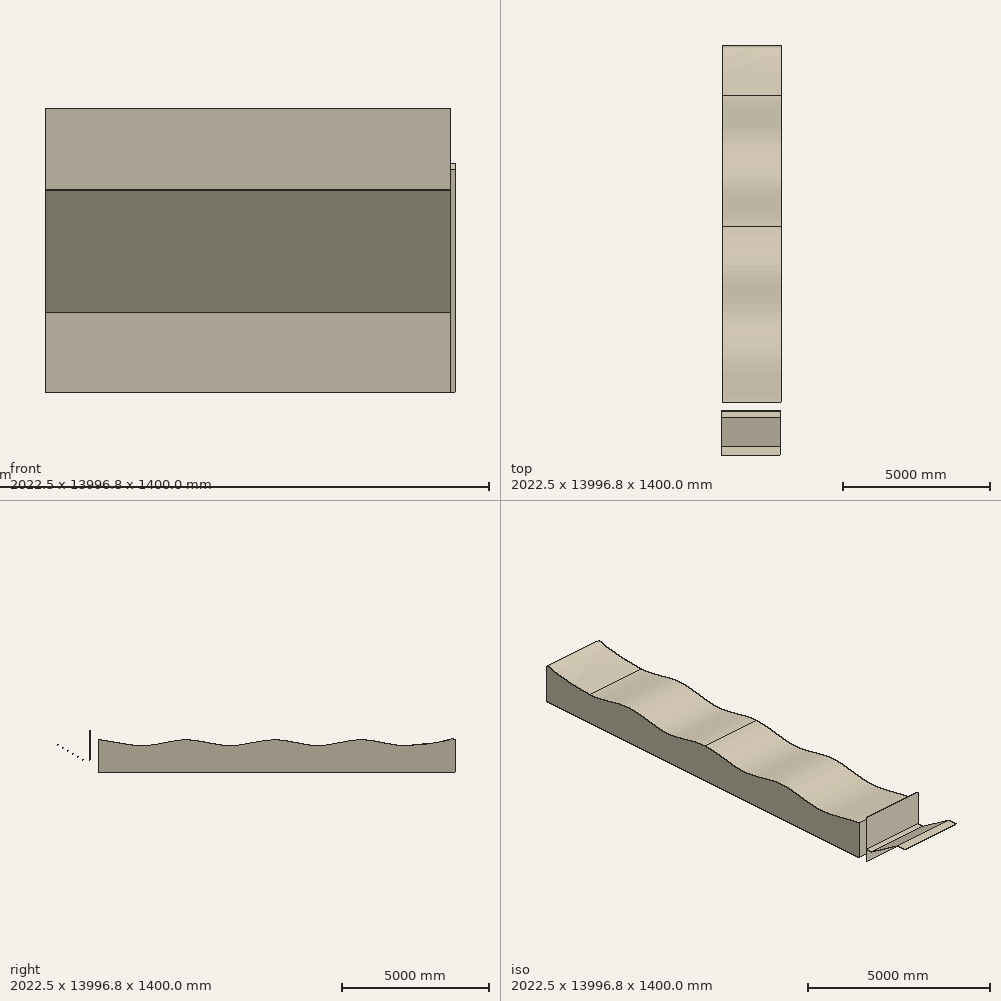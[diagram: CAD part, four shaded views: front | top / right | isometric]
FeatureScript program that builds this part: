
annotation { "Feature Type Name" : "Feature", "Feature Type Description" : "" }
export const myFeature = defineFeature(function(context is Context, id is Id, definition is map)
    precondition{}
    {
        {
            var Q0;
            Q0=qCreatedBy(makeId("Right.planeOp"),FACE);
            var sketch = newSketch(context, id + "F0", { "sketchPlane" : qUnion([Q0])});
            skLineSegment(sketch, "E0", {"start": v(0, 0) * mm, "end": v(0, 400) * mm});
            skLineSegment(sketch, "E1", {"start": v(0, 400) * mm, "end": v(-200, 400) * mm});
            skLineSegment(sketch, "E2", {"start": v(-200, 400) * mm, "end": v(-1200, 1000) * mm});
            skLineSegment(sketch, "E3", {"start": v(-1200, 1000) * mm, "end": v(-1500, 1000) * mm});
            skLineSegment(sketch, "E4.0", {"start": v(-1201.76, 993.65) * mm, "end": v(-1500, 993.65) * mm});
            skLineSegment(sketch, "E4.1", {"start": v(-201.76, 393.65) * mm, "end": v(-1201.76, 993.65) * mm});
            skLineSegment(sketch, "E4.2", {"start": v(-6.35, 393.65) * mm, "end": v(-201.76, 393.65) * mm});
            skLineSegment(sketch, "E4.3", {"start": v(-6.35, 0) * mm, "end": v(-6.35, 393.65) * mm});
            skLineSegment(sketch, "E5", {"start": v(-1500, 993.65) * mm, "end": v(-1500, 1000) * mm});
            skLineSegment(sketch, "E6", {"start": v(-6.35, 0) * mm, "end": v(0, 0) * mm});
            skSolve(sketch);
        }
        {
            var Q0;
            Q0=makeQuery(id+"F0.imprint","IMPRINT",FACE,{"disambiguationData":[TD([[makeQuery(id+"F0.imprint","IMPRINT",EDGE,{"derivedFrom":sQuery(id+"F0.wireOp",EDGE,"E0")}),1.0]])]});
            extrude(context, id + "F1", {"entities" : qUnion([Q0]), "endBound" : BoundingType.SYMMETRIC, "depth" : 2000 * mm});
        }
        {
            var Q0;
            Q0=makeQuery(id+"F1.opExtrude","SWEPT_FACE",FACE,{"disambiguationData":[OSD([sQuery(id+"F0.wireOp",EDGE,"E1")])]});
            var sketch = newSketch(context, id + "F2", { "sketchPlane" : qUnion([Q0])});
            skLineSegment(sketch, "E7.bottom", {"start": v(1000, 0) * mm, "end": v(-1000, 0) * mm});
            skLineSegment(sketch, "E7.top", {"start": v(1000, 23.09) * mm, "end": v(-1000, 23.09) * mm});
            skLineSegment(sketch, "E7.left", {"start": v(1000, 0) * mm, "end": v(1000, 23.09) * mm});
            skLineSegment(sketch, "E7.right", {"start": v(-1000, 0) * mm, "end": v(-1000, 23.09) * mm});
            skSolve(sketch);
        }
        {
            var Q0;
            Q0=makeQuery(id+"F2.imprint","IMPRINT",FACE,{"disambiguationData":[TD([[makeQuery(id+"F2.imprint","IMPRINT",EDGE,{"derivedFrom":sQuery(id+"F2.wireOp",EDGE,"E7.bottom")}),-1.0]])]});
            extrude(context, id + "F3", {"entities" : qUnion([Q0]), "depth" : 1000 * mm});
        }
        {
            var Q0;
            Q0=qCreatedBy(makeId("Top.planeOp"),FACE);
            var sketch = newSketch(context, id + "F4", { "sketchPlane" : qUnion([Q0])});
            skLineSegment(sketch, "E8.bottom", {"start": v(-977.46, 304.8) * mm, "end": v(1022.54, 304.8) * mm});
            skLineSegment(sketch, "E8.top", {"start": v(-977.46, 12496.8) * mm, "end": v(1022.54, 12496.8) * mm});
            skLineSegment(sketch, "E8.left", {"start": v(-977.46, 304.8) * mm, "end": v(-977.46, 12496.8) * mm});
            skLineSegment(sketch, "E8.right", {"start": v(1022.54, 304.8) * mm, "end": v(1022.54, 12496.8) * mm});
            skSolve(sketch);
        }
        {
            var Q0;
            Q0=makeQuery(id+"F4.imprint","IMPRINT",FACE,{"disambiguationData":[TD([[makeQuery(id+"F4.imprint","IMPRINT",EDGE,{"derivedFrom":sQuery(id+"F4.wireOp",EDGE,"E8.bottom")}),1.0]])]});
            extrude(context, id + "F5", {"entities" : qUnion([Q0]), "depth" : 1200 * mm, "offsetDistance" : 25.4 * mm});
        }
        {
            var Q0;
            Q0=makeQuery(id+"F5.opExtrude","SWEPT_FACE",FACE,{"disambiguationData":[OSD([sQuery(id+"F4.wireOp",EDGE,"E8.right")])]});
            var sketch = newSketch(context, id + "F6", { "sketchPlane" : qUnion([Q0])});
            skLineSegment(sketch, "E9", {"start": v(304.8, 1100) * mm, "end": v(304.8, 900) * mm, "construction": true});
            skLineSegment(sketch, "E10.1.0.0", {"start": v(1804.8, 1100) * mm, "end": v(1804.8, 900) * mm, "construction": true});
            skLineSegment(sketch, "E10.2.0.0", {"start": v(3304.8, 1100) * mm, "end": v(3304.8, 900) * mm, "construction": true});
            skLineSegment(sketch, "E10.3.0.0", {"start": v(4804.8, 1100) * mm, "end": v(4804.8, 900) * mm, "construction": true});
            skLineSegment(sketch, "E10.4.0.0", {"start": v(6304.8, 1100) * mm, "end": v(6304.8, 900) * mm, "construction": true});
            skLineSegment(sketch, "E10.5.0.0", {"start": v(7804.8, 1100) * mm, "end": v(7804.8, 900) * mm, "construction": true});
            skLineSegment(sketch, "E10.6.0.0", {"start": v(9304.8, 1100) * mm, "end": v(9304.8, 900) * mm, "construction": true});
            skLineSegment(sketch, "E10.7.0.0", {"start": v(10804.8, 1100) * mm, "end": v(10804.8, 900) * mm, "construction": true});
            skLineSegment(sketch, "E10.8.0.0", {"start": v(12304.8, 1100) * mm, "end": v(12304.8, 900) * mm, "construction": true});
            skLineSegment(sketch, "E10.9.0.0", {"start": v(13804.8, 1100) * mm, "end": v(13804.8, 900) * mm, "construction": true});
            skLineSegment(sketch, "E10.10.0.0", {"start": v(15304.8, 1100) * mm, "end": v(15304.8, 900) * mm, "construction": true});
            skLineSegment(sketch, "E10.11.0.0", {"start": v(16804.8, 1100) * mm, "end": v(16804.8, 900) * mm, "construction": true});
            skLineSegment(sketch, "E10.12.0.0", {"start": v(18304.8, 1100) * mm, "end": v(18304.8, 900) * mm, "construction": true});
            skLineSegment(sketch, "E10.13.0.0", {"start": v(19804.8, 1100) * mm, "end": v(19804.8, 900) * mm, "construction": true});
            skLineSegment(sketch, "E10.14.0.0", {"start": v(21304.8, 1100) * mm, "end": v(21304.8, 900) * mm, "construction": true});
            skLineSegment(sketch, "E10.15.0.0", {"start": v(22804.8, 1100) * mm, "end": v(22804.8, 900) * mm, "construction": true});
            skLineSegment(sketch, "E10.16.0.0", {"start": v(24304.8, 1100) * mm, "end": v(24304.8, 900) * mm, "construction": true});
            skLineSegment(sketch, "E10.17.0.0", {"start": v(25804.8, 1100) * mm, "end": v(25804.8, 900) * mm, "construction": true});
            skLineSegment(sketch, "E10.18.0.0", {"start": v(27304.8, 1100) * mm, "end": v(27304.8, 900) * mm, "construction": true});
            skLineSegment(sketch, "E10.19.0.0", {"start": v(28804.8, 1100) * mm, "end": v(28804.8, 900) * mm, "construction": true});
            skLineSegment(sketch, "E10.20.0.0", {"start": v(30304.8, 1100) * mm, "end": v(30304.8, 900) * mm, "construction": true});
            skLineSegment(sketch, "E10.21.0.0", {"start": v(31804.8, 1100) * mm, "end": v(31804.8, 900) * mm, "construction": true});
            skLineSegment(sketch, "E10.22.0.0", {"start": v(33304.8, 1100) * mm, "end": v(33304.8, 900) * mm, "construction": true});
            skLineSegment(sketch, "E10.23.0.0", {"start": v(34804.8, 1100) * mm, "end": v(34804.8, 900) * mm, "construction": true});
            skLineSegment(sketch, "E10.24.0.0", {"start": v(36304.8, 1100) * mm, "end": v(36304.8, 900) * mm, "construction": true});
            skLineSegment(sketch, "E10.direction1", {"start": v(304.8, 900) * mm, "end": v(1804.8, 900) * mm, "construction": true});
            skFitSpline(sketch, "E11", {"points": [v(304.8, 1100) * mm, v(1804.8, 900) * mm, v(3304.8, 1100) * mm, v(4804.8, 900) * mm, v(6304.8, 1100) * mm], "startDerivative": vector(3295.65, -19.13) * mm, "endDerivative": vector(6423.04, 137.76) * mm});
            skLineSegment(sketch, "E12", {"start": v(304.8, 1100) * mm, "end": v(304.8, 1200) * mm});
            skFitSpline(sketch, "E13", {"points": [v(6304.8, 1100) * mm, v(7804.8, 900) * mm, v(9304.8, 1100) * mm, v(10804.8, 900) * mm], "startDerivative": vector(4723.28, 56.77) * mm, "endDerivative": vector(4171.23, 112.94) * mm});
            skFitSpline(sketch, "E14", {"points": [v(10804.8, 900) * mm, v(12304.8, 1100) * mm, v(12496.8, 1100) * mm], "startDerivative": vector(2245.96, 51) * mm, "endDerivative": vector(1125.56, -606.88) * mm});
            skLineSegment(sketch, "E15", {"start": v(304.8, 1200) * mm, "end": v(12496.8, 1200) * mm});
            skLineSegment(sketch, "E16", {"start": v(12496.8, 1200) * mm, "end": v(12496.8, 1100) * mm});
            skSolve(sketch);
        }
        {
            var Q0;
            Q0=makeQuery(id+"F6.imprint","IMPRINT",FACE,{"disambiguationData":[TD([[makeQuery(id+"F6.imprint","IMPRINT",EDGE,{"derivedFrom":sQuery(id+"F6.wireOp",EDGE,"E11")}),1.0]])]});
            extrude(context, id + "F7", {"entities" : qUnion([Q0]), "operationType" : NewBodyOperationType.REMOVE, "endBound" : BoundingType.THROUGH_ALL, "oppositeDirection" : true, "depth" : 25.4 * mm, "offsetDistance" : 25.4 * mm});
        }
    });
